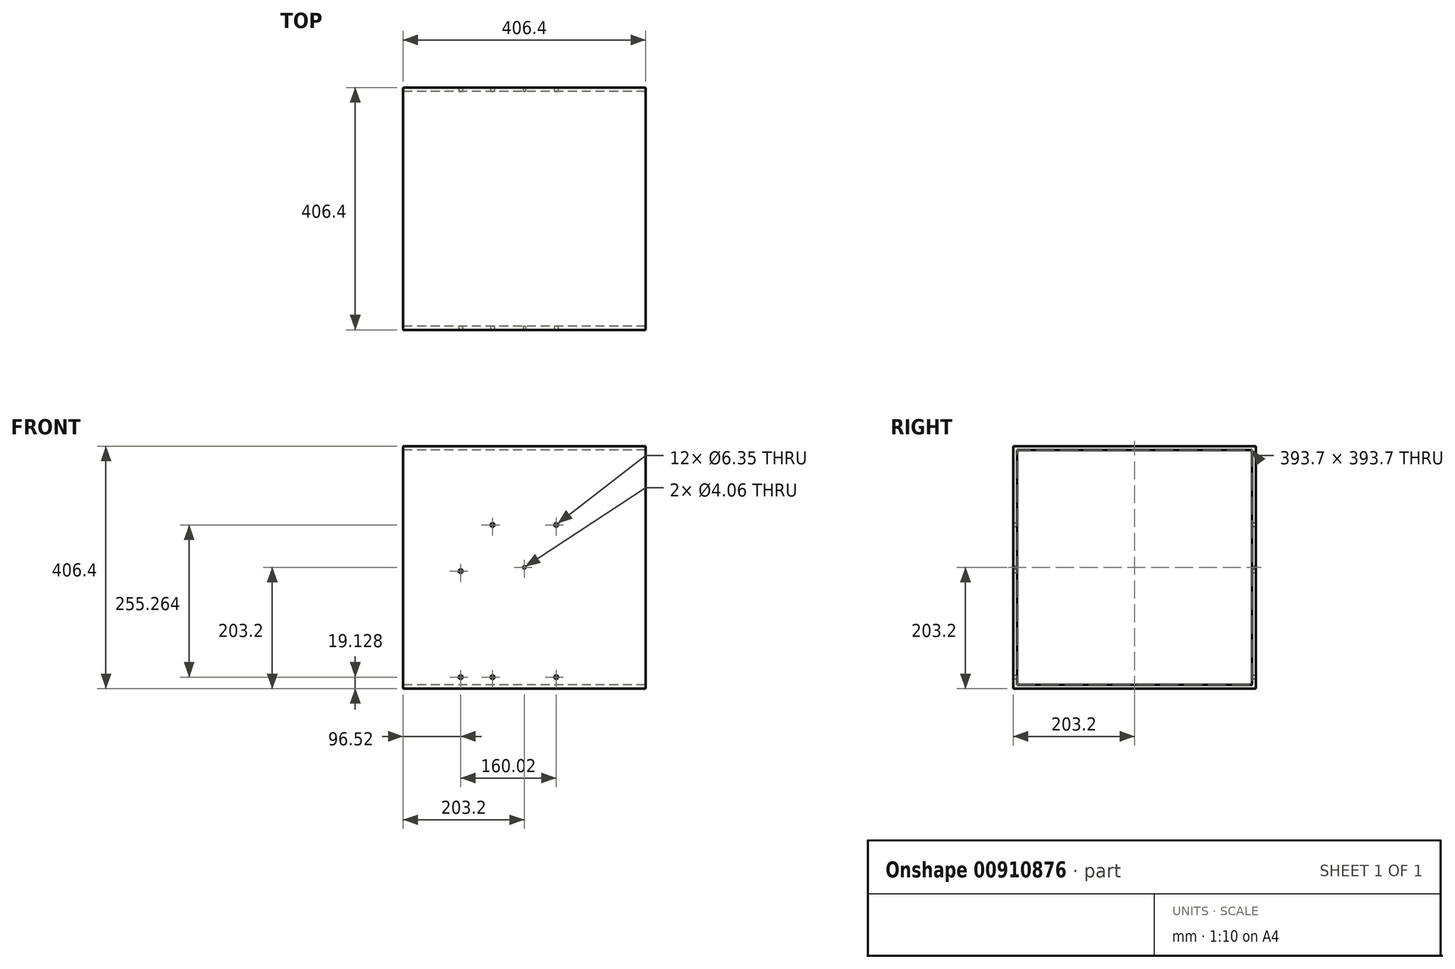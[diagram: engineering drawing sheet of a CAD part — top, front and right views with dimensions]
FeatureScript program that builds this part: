
annotation { "Feature Type Name" : "Feature", "Feature Type Description" : "" }
export const myFeature = defineFeature(function(context is Context, id is Id, definition is map)
    precondition{}
    {
        {
            var Q0;
            Q0=qCreatedBy(makeId("Right.planeOp"),FACE);
            var sketch = newSketch(context, id + "F0", { "sketchPlane" : qUnion([Q0])});
            skLineSegment(sketch, "E0.bottom", {"start": v(-203.2, 203.2) * mm, "end": v(203.2, 203.2) * mm});
            skLineSegment(sketch, "E0.top", {"start": v(-203.2, -203.2) * mm, "end": v(203.2, -203.2) * mm});
            skLineSegment(sketch, "E0.left", {"start": v(-203.2, 203.2) * mm, "end": v(-203.2, -203.2) * mm});
            skLineSegment(sketch, "E0.right", {"start": v(203.2, 203.2) * mm, "end": v(203.2, -203.2) * mm});
            skLineSegment(sketch, "E1", {"start": v(-203.2, 0) * mm, "end": v(0, 0) * mm, "construction": true});
            skLineSegment(sketch, "E2", {"start": v(0, 0) * mm, "end": v(0, 203.2) * mm, "construction": true});
            skLineSegment(sketch, "E3.bottom", {"start": v(-196.85, 196.85) * mm, "end": v(196.85, 196.85) * mm});
            skLineSegment(sketch, "E3.top", {"start": v(-196.85, -196.85) * mm, "end": v(196.85, -196.85) * mm});
            skLineSegment(sketch, "E3.left", {"start": v(-196.85, 196.85) * mm, "end": v(-196.85, -196.85) * mm});
            skLineSegment(sketch, "E3.right", {"start": v(196.85, 196.85) * mm, "end": v(196.85, -196.85) * mm});
            skLineSegment(sketch, "E4", {"start": v(0, 196.85) * mm, "end": v(0, 0) * mm, "construction": true});
            skLineSegment(sketch, "E5", {"start": v(0, 0) * mm, "end": v(-196.85, 0) * mm, "construction": true});
            skSolve(sketch);
        }
        {
            var Q0;
            Q0 = qSketchRegion(id + "F0", true);
            var Q1;
            Q1=makeQuery(id+"F0.imprint","IMPRINT",FACE,{"disambiguationData":[TD([[makeQuery(id+"F0.imprint","IMPRINT",EDGE,{"derivedFrom":sQuery(id+"F0.wireOp",EDGE,"E0.bottom")}),-1.0]])]});
            extrude(context, id + "F1", {"entities" : qUnion([Q0, Q1]), "depth" : 406.4 * mm, "offsetDistance" : 25.4 * mm});
        }
        {
            var Q0;
            Q0=makeQuery(id+"F1.opExtrude","SWEPT_FACE",FACE,{"disambiguationData":[OSD([sQuery(id+"F0.wireOp",EDGE,"E0.left")])]});
            var sketch = newSketch(context, id + "F2", { "sketchPlane" : qUnion([Q0])});
            skLineSegment(sketch, "E6", {"start": v(203.2, 203.2) * mm, "end": v(203.2, 0) * mm, "construction": true});
            skPoint(sketch, "E6.endSnap0", {"position": v(0, 0) * mm});
            skCircle(sketch, "E7", {"center": v(203.2, 0) * mm, "radius": 2.03 * mm});
            skLineSegment(sketch, "E8", {"start": v(96.52, 0) * mm, "end": v(203.2, 0) * mm, "construction": true});
            skCircle(sketch, "E9", {"center": v(96.52, -6.35) * mm, "radius": 6.35 * mm, "construction": true});
            skCircle(sketch, "E10", {"center": v(96.52, -6.35) * mm, "radius": 3.18 * mm});
            skLineSegment(sketch, "E11", {"start": v(203.2, 71.2) * mm, "end": v(250.2, 71.2) * mm, "construction": true});
            skCircle(sketch, "E12", {"center": v(256.54, 71.2) * mm, "radius": 6.35 * mm, "construction": true});
            skCircle(sketch, "E13", {"center": v(256.54, 71.2) * mm, "radius": 3.18 * mm});
            skCircle(sketch, "E14.MirrorC", {"center": v(149.86, 71.2) * mm, "radius": 3.18 * mm});
            skCircle(sketch, "E15", {"center": v(256.54, -184.07) * mm, "radius": 3.18 * mm});
            skCircle(sketch, "E16", {"center": v(149.86, -184.07) * mm, "radius": 3.18 * mm});
            skCircle(sketch, "E17", {"center": v(96.52, -184.07) * mm, "radius": 3.18 * mm});
            skSolve(sketch);
        }
        {
            var Q0;
            Q0=makeQuery(id+"F2.imprint","IMPRINT",FACE,{"disambiguationData":[TD([[makeQuery(id+"F2.imprint","IMPRINT",EDGE,{"derivedFrom":sQuery(id+"F2.wireOp",EDGE,"E7")}),-1.0]])]});
            extrude(context, id + "F3", {"entities" : qUnion([Q0]), "operationType" : NewBodyOperationType.INTERSECT, "oppositeDirection" : true, "depth" : 406.4 * mm, "offsetDistance" : 25.4 * mm});
        }
    });
